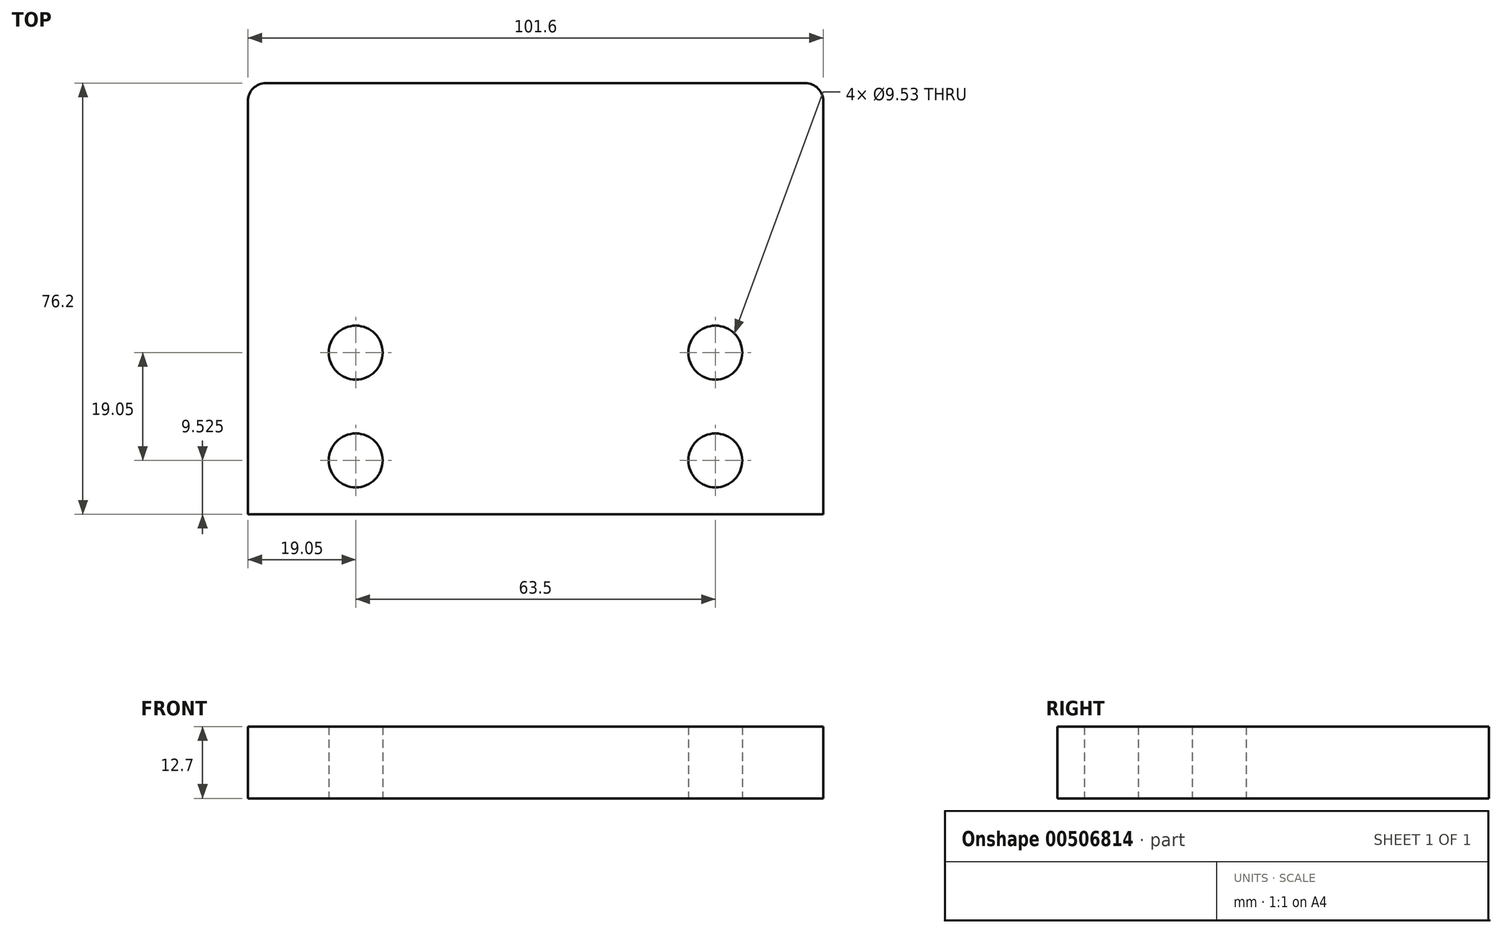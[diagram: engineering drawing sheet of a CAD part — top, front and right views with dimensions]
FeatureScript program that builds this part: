
annotation { "Feature Type Name" : "Feature", "Feature Type Description" : "" }
export const myFeature = defineFeature(function(context is Context, id is Id, definition is map)
    precondition{}
    {
        {
            var Q0;
            Q0=qCreatedBy(makeId("Top.planeOp"),FACE);
            var sketch = newSketch(context, id + "F0", { "sketchPlane" : qUnion([Q0])});
            skLineSegment(sketch, "E0.bottom", {"start": v(0, 0) * mm, "end": v(101.6, 0) * mm});
            skLineSegment(sketch, "E0.top", {"start": v(3.17, 76.2) * mm, "end": v(98.42, 76.2) * mm});
            skLineSegment(sketch, "E0.left", {"start": v(0, 0) * mm, "end": v(0, 73.03) * mm});
            skLineSegment(sketch, "E0.right", {"start": v(101.6, 0) * mm, "end": v(101.6, 73.03) * mm});
            skLineSegment(sketch, "E1.bottom", {"start": v(19.05, 28.58) * mm, "end": v(82.55, 28.58) * mm, "construction": true});
            skLineSegment(sketch, "E1.top", {"start": v(19.05, 9.53) * mm, "end": v(82.55, 9.53) * mm, "construction": true});
            skLineSegment(sketch, "E1.left", {"start": v(19.05, 28.58) * mm, "end": v(19.05, 9.53) * mm, "construction": true});
            skLineSegment(sketch, "E1.right", {"start": v(82.55, 28.58) * mm, "end": v(82.55, 9.53) * mm, "construction": true});
            skCircle(sketch, "E2", {"center": v(19.05, 28.58) * mm, "radius": 4.76 * mm});
            skCircle(sketch, "E3", {"center": v(19.05, 9.53) * mm, "radius": 4.76 * mm});
            skCircle(sketch, "E4", {"center": v(82.55, 9.53) * mm, "radius": 4.76 * mm});
            skCircle(sketch, "E5", {"center": v(82.55, 28.58) * mm, "radius": 4.76 * mm});
            skPoint(sketch, "E6.visualSharp", {"position": v(0, 76.2) * mm});
            skArc(sketch, "E6.filletArc", {"start": v(3.17, 76.2) * mm, "mid": v(0.93, 75.27) * mm, "end": v(0, 73.03) * mm});
            skPoint(sketch, "E7.visualSharp", {"position": v(101.6, 76.2) * mm});
            skArc(sketch, "E7.filletArc", {"start": v(101.6, 73.03) * mm, "mid": v(100.67, 75.27) * mm, "end": v(98.42, 76.2) * mm});
            skSolve(sketch);
        }
        {
            var Q0;
            Q0 = qSketchRegion(id + "F0", true);
            extrude(context, id + "F1", {"entities" : qUnion([Q0]), "depth" : 12.7 * mm});
        }
    });
